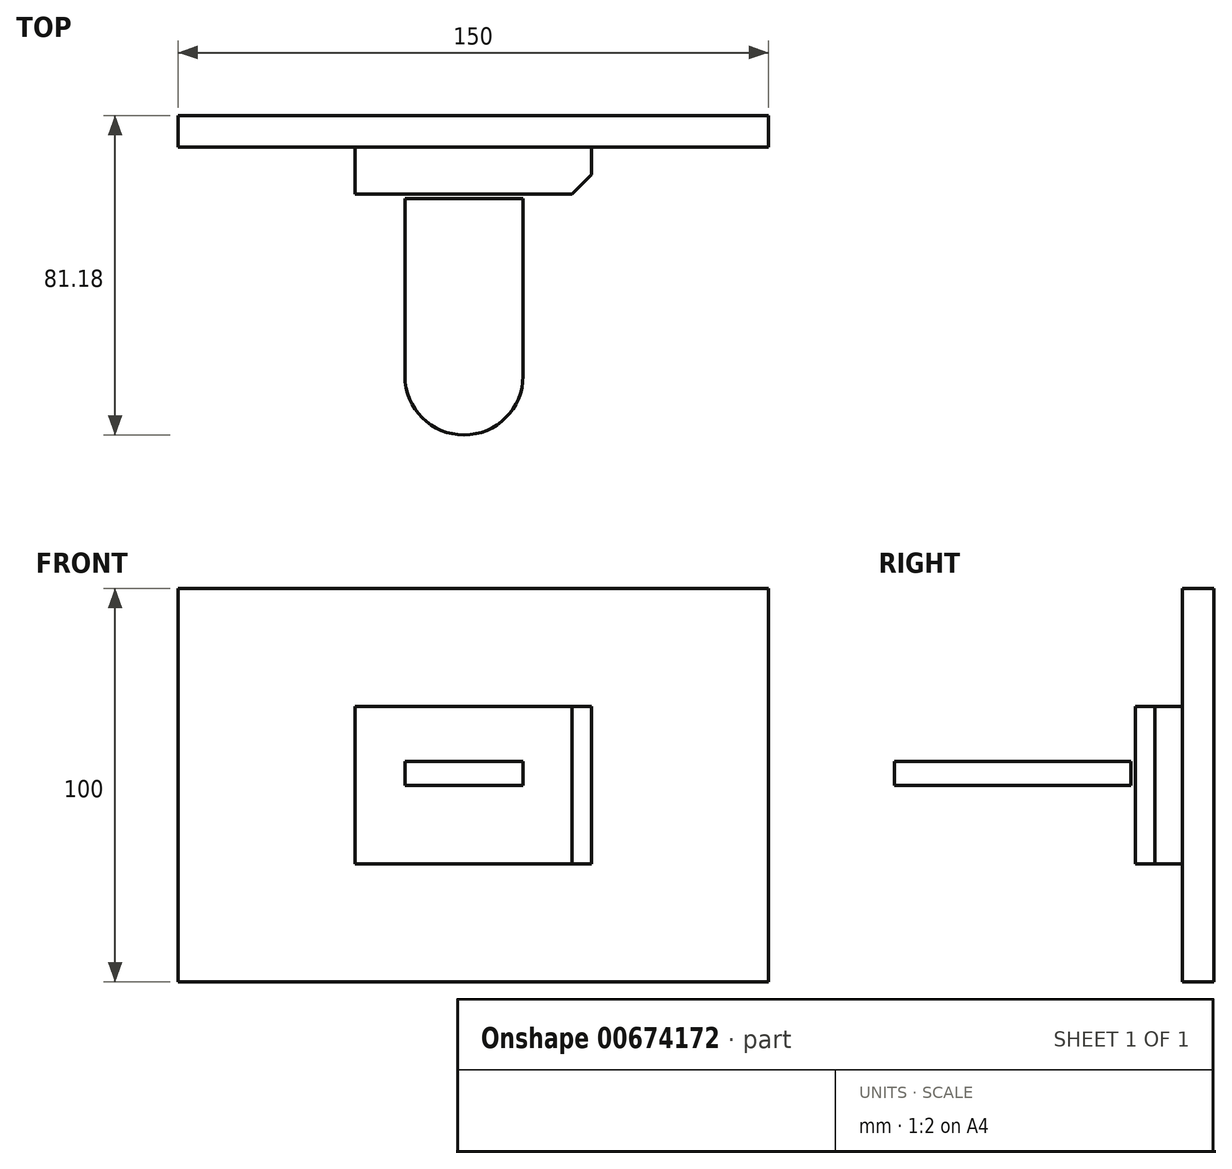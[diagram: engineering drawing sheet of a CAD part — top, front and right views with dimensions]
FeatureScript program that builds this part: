
annotation { "Feature Type Name" : "Feature", "Feature Type Description" : "" }
export const myFeature = defineFeature(function(context is Context, id is Id, definition is map)
    precondition{}
    {
        {
            var Q0;
            Q0=qCreatedBy(makeId("Front.planeOp"),FACE);
            var sketch = newSketch(context, id + "F0", { "sketchPlane" : qUnion([Q0])});
            skLineSegment(sketch, "E0.bottom", {"start": v(75, -50) * mm, "end": v(-75, -50) * mm});
            skLineSegment(sketch, "E0.top", {"start": v(75, 50) * mm, "end": v(-75, 50) * mm});
            skLineSegment(sketch, "E0.left", {"start": v(75, -50) * mm, "end": v(75, 50) * mm});
            skLineSegment(sketch, "E0.right", {"start": v(-75, -50) * mm, "end": v(-75, 50) * mm});
            skPoint(sketch, "E0.middle", {"position": v(0, 0) * mm});
            skSolve(sketch);
        }
        {
            var Q0;
            Q0=makeQuery(id+"F0.imprint","IMPRINT",FACE,{"disambiguationData":[TD([[makeQuery(id+"F0.imprint","IMPRINT",EDGE,{"derivedFrom":sQuery(id+"F0.wireOp",EDGE,"E0.bottom")}),-1.0]])]});
            extrude(context, id + "F1", {"entities" : qUnion([Q0]), "depth" : 3 * mm, "offsetDistance" : 25 * mm});
        }
        {
            var Q0;
            Q0=makeQuery(id+"F1.opExtrude","CAP_FACE",FACE,{"disambiguationData":[OSD([sQuery(id+"F0.wireOp",EDGE,"E0.bottom"),sQuery(id+"F0.wireOp",EDGE,"E0.top"),sQuery(id+"F0.wireOp",EDGE,"E0.left"),sQuery(id+"F0.wireOp",EDGE,"E0.right")])],"isStart":false});
            extrude(context, id + "F2", {"entities" : qUnion([Q0]), "operationType" : NewBodyOperationType.ADD, "depth" : 5 * mm, "offsetDistance" : 25 * mm});
        }
        {
            var Q0;
            Q0=qCreatedBy(makeId("Front.planeOp"),FACE);
            var sketch = newSketch(context, id + "F3", { "sketchPlane" : qUnion([Q0])});
            skLineSegment(sketch, "E1.bottom", {"start": v(30, -20) * mm, "end": v(-30, -20) * mm});
            skLineSegment(sketch, "E1.top", {"start": v(30, 20) * mm, "end": v(-30, 20) * mm});
            skLineSegment(sketch, "E1.left", {"start": v(30, -20) * mm, "end": v(30, 20) * mm});
            skLineSegment(sketch, "E1.right", {"start": v(-30, -20) * mm, "end": v(-30, 20) * mm});
            skPoint(sketch, "E1.middle", {"position": v(0, 0) * mm});
            skSolve(sketch);
        }
        {
            var Q0;
            Q0 = qSketchRegion(id + "F3", true);
            extrude(context, id + "F4", {"entities" : qUnion([Q0]), "operationType" : NewBodyOperationType.ADD, "depth" : 10 * mm, "offsetDistance" : 25 * mm});
        }
        {
            var Q0;
            Q0=makeQuery(id+"F4.opExtrude","CAP_FACE",FACE,{"disambiguationData":[OSD([sQuery(id+"F3.wireOp",EDGE,"E1.bottom"),sQuery(id+"F3.wireOp",EDGE,"E1.top"),sQuery(id+"F3.wireOp",EDGE,"E1.left"),sQuery(id+"F3.wireOp",EDGE,"E1.right")])],"isStart":false});
            extrude(context, id + "F5", {"entities" : qUnion([Q0]), "operationType" : NewBodyOperationType.ADD, "depth" : 10 * mm, "offsetDistance" : 25 * mm});
        }
        {
            var Q0;
            Q0=makeQuery(id+"F5.opExtrude","CAP_EDGE",EDGE,{"disambiguationData":[OSD([sQuery(id+"F3.wireOp",EDGE,"E1.left")])],"isStart":false});
            chamfer(context, id + "F6", {"entities" : qUnion([Q0]), "width" : 5 * mm, "tangentPropagation" : true});
        }
        {
            var Q0;
            Q0=qCreatedBy(makeId("Top.planeOp"),FACE);
            var sketch = newSketch(context, id + "F7", { "sketchPlane" : qUnion([Q0])});
            skLineSegment(sketch, "E2.bottom", {"start": v(-17.38, -81.18) * mm, "end": v(12.62, -81.18) * mm});
            skLineSegment(sketch, "E2.top", {"start": v(-17.38, -21.18) * mm, "end": v(12.62, -21.18) * mm});
            skLineSegment(sketch, "E2.left", {"start": v(-17.38, -81.18) * mm, "end": v(-17.38, -21.18) * mm});
            skLineSegment(sketch, "E2.right", {"start": v(12.62, -81.18) * mm, "end": v(12.62, -21.18) * mm});
            skSolve(sketch);
        }
        {
            var Q0;
            Q0 = qSketchRegion(id + "F7", true);
            extrude(context, id + "F8", {"entities" : qUnion([Q0]), "depth" : 6 * mm, "offsetDistance" : 25 * mm});
        }
        {
            var Q0;
            Q0=makeQuery(id+"F8.opExtrude","SWEPT_EDGE",EDGE,{"disambiguationData":[OSD([sQuery(id+"F7.wireOp",EDGE,"E2.bottom"),sQuery(id+"F7.wireOp",EDGE,"E2.right")])]});
            var Q1;
            Q1=makeQuery(id+"F8.opExtrude","SWEPT_EDGE",EDGE,{"disambiguationData":[OSD([sQuery(id+"F7.wireOp",EDGE,"E2.bottom"),sQuery(id+"F7.wireOp",EDGE,"E2.left")])]});
            fillet(context, id + "F9", {"entities" : qUnion([Q0, Q1]), "radius" : 15 * mm, "tangentPropagation" : true, "allowEdgeOverflow" : false});
        }
    });
